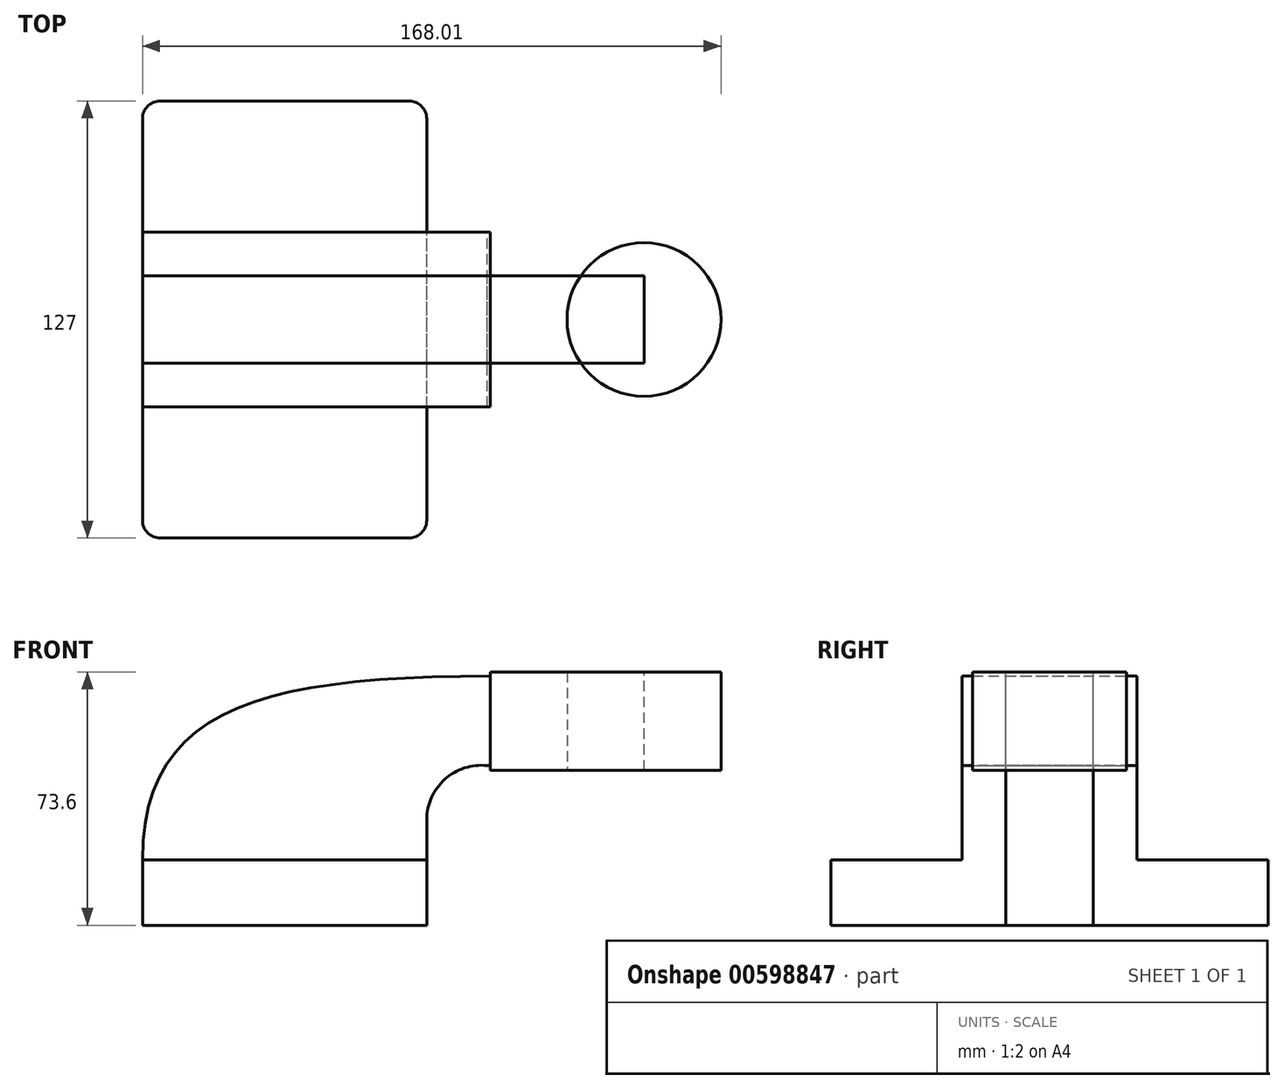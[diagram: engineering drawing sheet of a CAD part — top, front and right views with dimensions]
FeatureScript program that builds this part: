
annotation { "Feature Type Name" : "Feature", "Feature Type Description" : "" }
export const myFeature = defineFeature(function(context is Context, id is Id, definition is map)
    precondition{}
    {
        {
            var Q0;
            Q0=qCreatedBy(makeId("Front.planeOp"),FACE);
            var sketch = newSketch(context, id + "F0", { "sketchPlane" : qUnion([Q0])});
            skLineSegment(sketch, "E0.bottom", {"start": v(-41.28, -9.52) * mm, "end": v(41.28, -9.52) * mm});
            skLineSegment(sketch, "E0.top", {"start": v(-41.28, 9.52) * mm, "end": v(41.28, 9.52) * mm});
            skLineSegment(sketch, "E0.left", {"start": v(-41.28, -9.52) * mm, "end": v(-41.28, 9.53) * mm});
            skLineSegment(sketch, "E0.right", {"start": v(41.28, -9.52) * mm, "end": v(41.28, 9.52) * mm});
            skPoint(sketch, "E0.middle", {"position": v(0, 0) * mm});
            skLineSegment(sketch, "E1", {"start": v(41.28, 9.52) * mm, "end": v(41.28, 21.07) * mm});
            skLineSegment(sketch, "E2.2", {"start": v(22.23, 11.87) * mm, "end": v(22.23, 21.07) * mm});
            skLineSegment(sketch, "E3", {"start": v(85.91, 54.9) * mm, "end": v(85.73, 49.78) * mm});
            skArc(sketch, "E4", {"start": v(41.28, 21.07) * mm, "mid": v(46.56, 32.9) * mm, "end": v(58.89, 36.88) * mm});
            skLineSegment(sketch, "E5.bottom", {"start": v(104.38, 35.5) * mm, "end": v(59.68, 35.5) * mm});
            skLineSegment(sketch, "E5.top", {"start": v(104.38, 64.07) * mm, "end": v(59.68, 64.07) * mm});
            skLineSegment(sketch, "E5.left", {"start": v(104.38, 35.5) * mm, "end": v(104.38, 64.07) * mm});
            skLineSegment(sketch, "E5.right", {"start": v(59.68, 35.5) * mm, "end": v(59.68, 64.07) * mm});
            skPoint(sketch, "E5.middle", {"position": v(82.03, 49.78) * mm});
            skLineSegment(sketch, "E6", {"start": v(82.03, 35.5) * mm, "end": v(82.03, 64.07) * mm});
            skArc(sketch, "E7", {"start": v(22.23, 21.07) * mm, "mid": v(32.96, 49.15) * mm, "end": v(59.68, 62.9) * mm});
            skLineSegment(sketch, "E8", {"start": v(59.68, 62.9) * mm, "end": v(82.03, 62.9) * mm});
            skLineSegment(sketch, "E9", {"start": v(58.89, 36.88) * mm, "end": v(82.03, 36.88) * mm});
            skFitSpline(sketch, "E10", {"points": [v(-41.28, 9.53) * mm, v(59.68, 62.9) * mm], "startDerivative": vector(0.56, 131.17) * mm, "endDerivative": vector(202.38, 0.3) * mm});
            skSolve(sketch);
        }
        {
            var Q0;
            Q0=makeQuery(id+"F0.imprint","IMPRINT",FACE,{"disambiguationData":[TD([[makeQuery(id+"F0.imprint","IMPRINT",EDGE,{"derivedFrom":sQuery(id+"F0.wireOp",EDGE,"E0.bottom")}),1.0]])]});
            extrude(context, id + "F1", {"entities" : qUnion([Q0]), "endBound" : BoundingType.SYMMETRIC, "depth" : 127 * mm, "offsetDistance" : 25.4 * mm});
        }
        {
            var Q0;
            {var subQ1=sQuery(id+"F0.wireOp",EDGE,"E1");Q0=makeQuery(id+"F0.imprint","IMPRINT",FACE,{"disambiguationData":[TD([[makeQuery(id+"F0.imprint","IMPRINT",EDGE,{"derivedFrom":subQ1}),1.0]])]});}
            var Q1;
            {var subQ8=sQuery(id+"F0.wireOp",EDGE,"z1Z4sH1g-h4O8-algI-ZzNQ-71Qvpzj8HZ7F.bottom");Q1=makeQuery(id+"F0.imprint","IMPRINT",FACE,{"disambiguationData":[TD([[makeQuery(id+"F0.imprint","IMPRINT",EDGE,{"derivedFrom":subQ8}),1.0]])]});}
            extrude(context, id + "F2", {"entities" : qUnion([Q0, Q1]), "operationType" : NewBodyOperationType.ADD, "endBound" : BoundingType.SYMMETRIC, "depth" : 50.8 * mm, "offsetDistance" : 25.4 * mm});
        }
        {
            var Q0;
            {var subQ4=sQuery(id+"F0.wireOp",EDGE,"E5.left");Q0=makeQuery(id+"F0.imprint","IMPRINT",FACE,{"disambiguationData":[TD([[makeQuery(id+"F0.imprint","IMPRINT",EDGE,{"derivedFrom":subQ4}),1.0]])]});}
            var Q1;
            Q1=sQuery(id+"F0.wireOp",EDGE,"E5.left");
            revolve(context, id + "F3", {"entities" : qUnion([Q0]), "axis" : qUnion([Q1]), "revolveType" : RevolveType.FULL});
        }
        {
            var Q0;
            Q0=makeQuery(id+"F1.opExtrude","CAP_EDGE",EDGE,{"disambiguationData":[OSD([sQuery(id+"F0.wireOp",EDGE,"E0.right")])],"isStart":false});
            var Q1;
            Q1=makeQuery(id+"F1.opExtrude","CAP_EDGE",EDGE,{"disambiguationData":[OSD([sQuery(id+"F0.wireOp",EDGE,"E0.left")])],"isStart":false});
            var Q2;
            Q2=makeQuery(id+"F1.opExtrude","CAP_EDGE",EDGE,{"disambiguationData":[OSD([sQuery(id+"F0.wireOp",EDGE,"E0.right")])],"isStart":true});
            var Q3;
            Q3=makeQuery(id+"F1.opExtrude","CAP_EDGE",EDGE,{"disambiguationData":[OSD([sQuery(id+"F0.wireOp",EDGE,"E0.left")])],"isStart":true});
            fillet(context, id + "F4", {"entities" : qUnion([Q0, Q1, Q2, Q3]), "radius" : 5.08 * mm, "tangentPropagation" : true, "allowEdgeOverflow" : false});
        }
        {
            var Q0;
            Q0 = qSketchRegion(id + "F0", true);
            extrude(context, id + "F5", {"entities" : qUnion([Q0]), "endBound" : BoundingType.SYMMETRIC, "depth" : 25.4 * mm, "offsetDistance" : 25.4 * mm});
        }
    });
